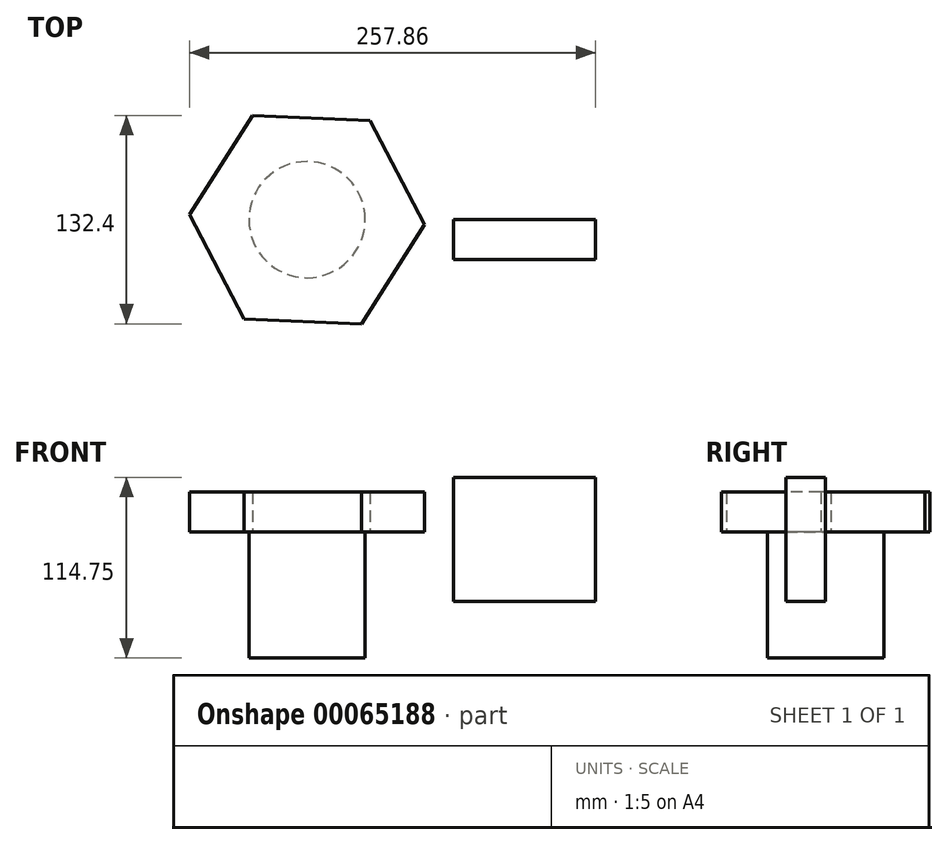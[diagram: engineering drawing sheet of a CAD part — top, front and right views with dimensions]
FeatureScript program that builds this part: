
annotation { "Feature Type Name" : "Feature", "Feature Type Description" : "" }
export const myFeature = defineFeature(function(context is Context, id is Id, definition is map)
    precondition{}
    {
        {
            var Q0;
            Q0=qCreatedBy(makeId("Top.planeOp"),FACE);
            var sketch = newSketch(context, id + "F0", { "sketchPlane" : qUnion([Q0])});
            skCircle(sketch, "E0.cCircle", {"center": v(0, 0) * mm, "radius": 64.67 * mm, "construction": true});
            skLineSegment(sketch, "E0.0", {"start": v(40.05, 63.03) * mm, "end": v(74.6, -3.17) * mm});
            skLineSegment(sketch, "E0.1", {"start": v(74.6, -3.17) * mm, "end": v(34.56, -66.2) * mm});
            skLineSegment(sketch, "E0.2", {"start": v(34.56, -66.2) * mm, "end": v(-40.05, -63.03) * mm});
            skLineSegment(sketch, "E0.3", {"start": v(-40.05, -63.03) * mm, "end": v(-74.6, 3.17) * mm});
            skLineSegment(sketch, "E0.4", {"start": v(-74.6, 3.17) * mm, "end": v(-34.56, 66.2) * mm});
            skLineSegment(sketch, "E0.5", {"start": v(-34.56, 66.2) * mm, "end": v(40.05, 63.03) * mm});
            skPoint(sketch, "E0.0.midPoint", {"position": v(57.33, 29.93) * mm});
            skSolve(sketch);
        }
        {
            var Q0;
            Q0=makeQuery(id+"F0.imprint","IMPRINT",FACE,{"disambiguationData":[TD([[makeQuery(id+"F0.imprint","IMPRINT",EDGE,{"derivedFrom":sQuery(id+"F0.wireOp",EDGE,"E0.0")}),-1.0]])]});
            extrude(context, id + "F1", {"entities" : qUnion([Q0]), "depth" : 25.4 * mm});
        }
        {
            var Q0;
            Q0=makeQuery(id+"F1.opExtrude","CAP_FACE",FACE,{"disambiguationData":[OSD([sQuery(id+"F0.wireOp",EDGE,"E0.0"),sQuery(id+"F0.wireOp",EDGE,"E0.1"),sQuery(id+"F0.wireOp",EDGE,"E0.2"),sQuery(id+"F0.wireOp",EDGE,"E0.3"),sQuery(id+"F0.wireOp",EDGE,"E0.4"),sQuery(id+"F0.wireOp",EDGE,"E0.5")])],"isStart":true});
            var sketch = newSketch(context, id + "F2", { "sketchPlane" : qUnion([Q0])});
            skCircle(sketch, "E1", {"center": v(0, 0) * mm, "radius": 36.91 * mm});
            skSolve(sketch);
        }
        {
            var Q0;
            Q0=makeQuery(id+"F2.imprint","IMPRINT",FACE,{"disambiguationData":[TD([[makeQuery(id+"F2.imprint","IMPRINT",EDGE,{"derivedFrom":sQuery(id+"F2.wireOp",EDGE,"E1")}),1.0]])]});
            extrude(context, id + "F3", {"entities" : qUnion([Q0]), "operationType" : NewBodyOperationType.ADD, "depth" : 80 * mm});
        }
        {
            var Q0;
            Q0=qCreatedBy(makeId("Front.planeOp"),FACE);
            var sketch = newSketch(context, id + "F4", { "sketchPlane" : qUnion([Q0])});
            skLineSegment(sketch, "E2.bottom", {"start": v(183.25, 34.75) * mm, "end": v(93.06, 34.75) * mm});
            skLineSegment(sketch, "E2.top", {"start": v(183.25, -44.03) * mm, "end": v(93.06, -44.03) * mm});
            skLineSegment(sketch, "E2.left", {"start": v(183.25, 34.75) * mm, "end": v(183.25, -44.03) * mm});
            skLineSegment(sketch, "E2.right", {"start": v(93.06, 34.75) * mm, "end": v(93.06, -44.03) * mm});
            skSolve(sketch);
        }
        {
            var Q0;
            Q0 = qSketchRegion(id + "F4", true);
            extrude(context, id + "F5", {"entities" : qUnion([Q0]), "depth" : 25.4 * mm});
        }
    });
